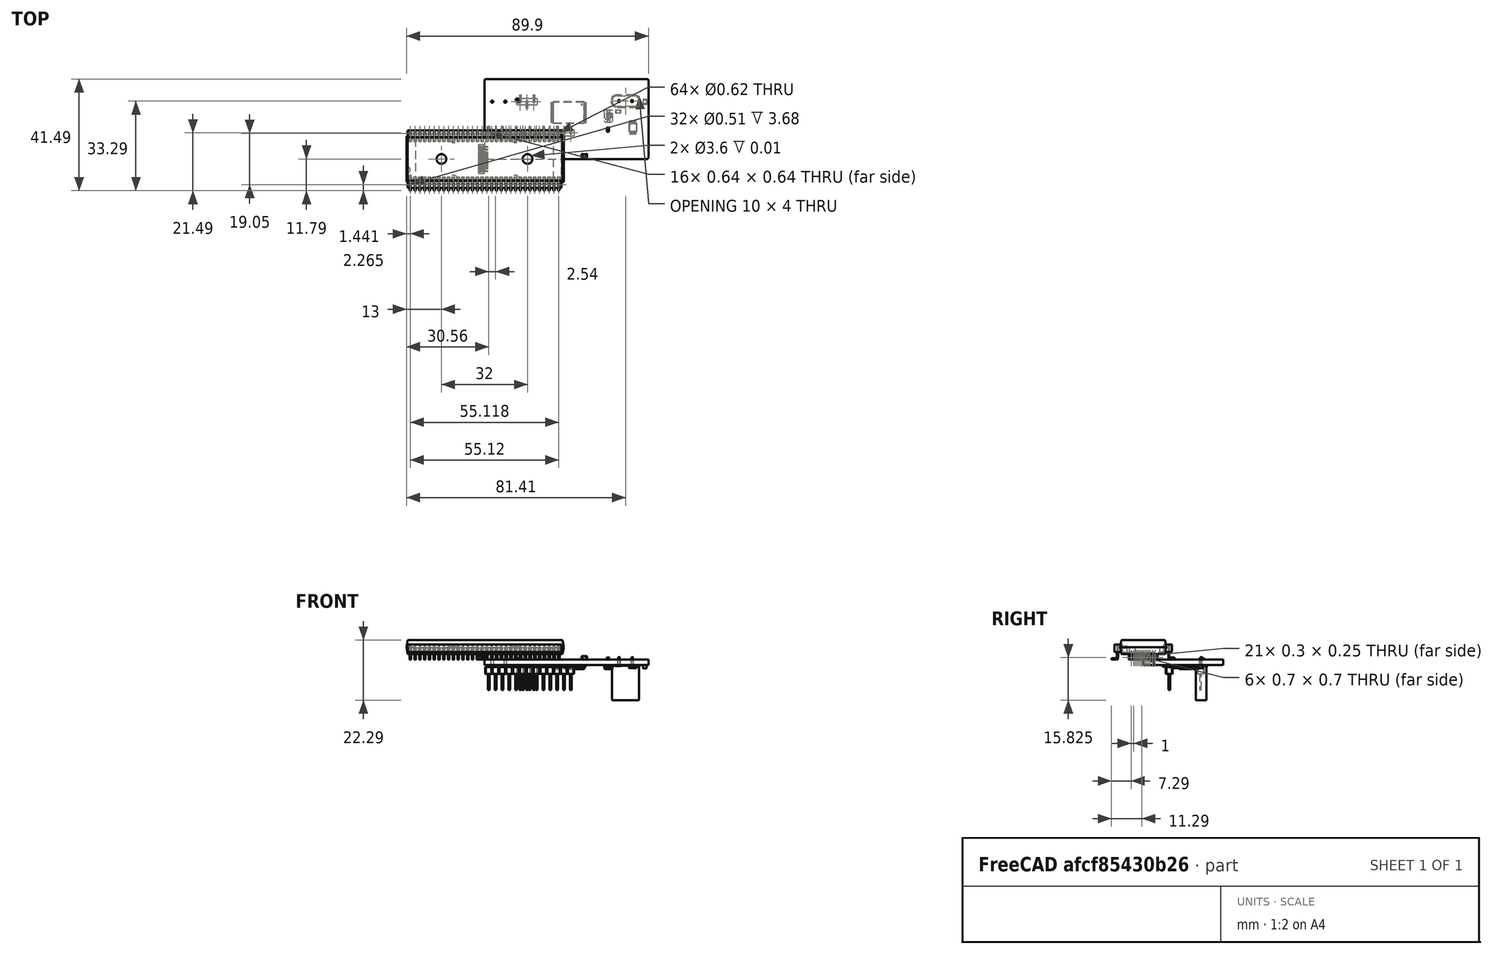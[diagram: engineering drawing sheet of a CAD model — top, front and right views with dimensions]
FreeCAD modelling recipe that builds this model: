
FCSTD DOCUMENT  (FreeCAD 0.20R29177 (Git))
Label: Ultra-MSX-VDP-socket-type
License: All rights reserved
LicenseURL: http://en.wikipedia.org/wiki/All_rights_reserved
objects: Part::Feature×145, App::Link×55, App::Part×24, PartDesign::CoordinateSystem×1, Sketcher::SketchObject×1
note: 147 computed .brp shape members not serialized (recipe doc carries the construction recipe); baked Part::Feature solids carry a one-line shape summary decoded from their .brp

FEATURE [PartDesign::CoordinateSystem] Local_CS_a649
  AttacherType = Attacher::AttachEngine3D
FEATURE [Part::Feature] Pcb_a649
  Placement = pos=(-95.1,117.3,0) rot=(0,0,1;0rad)
  shape: bbox 60.9 x 29.7 x 2 mm, 14 faces (baked)
FEATURE [Sketcher::SketchObject] PCB_Sketch_a649
  FullyConstrained = false
  sketch-geometry (8):
    g0: LineSegment StartX=60.4 StartY=29.7 StartZ=0 EndX=0.5 EndY=29.7 EndZ=0
    g1: LineSegment StartX=0 StartY=29.2 StartZ=0 EndX=1e-16 EndY=0.5 EndZ=0
    g2: LineSegment StartX=0.5 StartY=0 StartZ=0 EndX=60.4 EndY=-1.3e-15 EndZ=0
    g3: LineSegment StartX=60.9 StartY=0.5 StartZ=0 EndX=60.9 EndY=29.2 EndZ=0
    g4: ArcOfCircle CenterX=0.500001 CenterY=29.2 CenterZ=0 NormalX=0 NormalY=0 NormalZ=-1 AngleXU=2.66714e-06 Radius=0.500001 StartAngle=0 EndAngle=1.57079
    g5: ArcOfCircle CenterX=60.4 CenterY=0.500001 CenterZ=0 NormalX=0 NormalY=0 NormalZ=-1 AngleXU=-3.14159 Radius=0.500001 StartAngle=0 EndAngle=1.57079
    g6: ArcOfCircle CenterX=0.500001 CenterY=0.500001 CenterZ=0 NormalX=0 NormalY=0 NormalZ=-1 AngleXU=-1.57079 Radius=0.500001 StartAngle=0 EndAngle=1.57079
    g7: ArcOfCircle CenterX=60.4 CenterY=29.2 CenterZ=0 NormalX=0 NormalY=0 NormalZ=-1 AngleXU=1.5708 Radius=0.500001 StartAngle=0 EndAngle=1.57079
  constraints (8):
    c: Coincident(g1,g6)
    c: Coincident(g1,g4)
    c: Coincident(g2,g6)
    c: Coincident(g0,g4)
    c: Coincident(g2,g5)
    c: Coincident(g0,g7)
    c: Coincident(g3,g5)
    c: Coincident(g3,g7)
FEATURE [Part::Feature] Part__Feature  label="base-pin002"
  shape: bbox 0.62 x 2.57 x 5.591 mm, 71 faces (baked)
FEATURE [Part::Feature] Part__Feature001  label="base-pin003"
  Placement = pos=(1.778,0,0) rot=(0,0,1;0rad)
  shape: bbox 0.62 x 2.57 x 5.591 mm, 71 faces (baked)
FEATURE [Part::Feature] Part__Feature002  label="base-pin004"
  Placement = pos=(3.556,0,0) rot=(0,0,1;0rad)
  shape: bbox 0.62 x 2.57 x 5.591 mm, 71 faces (baked)
FEATURE [Part::Feature] Part__Feature003  label="base-pin005"
  Placement = pos=(5.334,0,0) rot=(0,0,1;0rad)
  shape: bbox 0.62 x 2.57 x 5.591 mm, 71 faces (baked)
FEATURE [Part::Feature] Part__Feature004  label="base-pin006"
  Placement = pos=(7.112,0,0) rot=(0,0,1;0rad)
  shape: bbox 0.62 x 2.57 x 5.591 mm, 71 faces (baked)
FEATURE [Part::Feature] Part__Feature005  label="base-pin007"
  Placement = pos=(8.89,0,0) rot=(0,0,1;0rad)
  shape: bbox 0.62 x 2.57 x 5.591 mm, 71 faces (baked)
FEATURE [Part::Feature] Part__Feature006  label="base-pin008"
  Placement = pos=(10.668,0,0) rot=(0,0,1;0rad)
  shape: bbox 0.62 x 2.57 x 5.591 mm, 71 faces (baked)
FEATURE [Part::Feature] Part__Feature007  label="base-pin009"
  Placement = pos=(12.446,0,0) rot=(0,0,1;0rad)
  shape: bbox 0.62 x 2.57 x 5.591 mm, 71 faces (baked)
FEATURE [Part::Feature] Part__Feature008  label="base-pin010"
  Placement = pos=(14.224,0,0) rot=(0,0,1;0rad)
  shape: bbox 0.62 x 2.57 x 5.591 mm, 71 faces (baked)
FEATURE [Part::Feature] Part__Feature009  label="base-pin011"
  Placement = pos=(16.002,0,0) rot=(0,0,1;0rad)
  shape: bbox 0.62 x 2.57 x 5.591 mm, 71 faces (baked)
FEATURE [Part::Feature] Part__Feature010  label="base-pin012"
  Placement = pos=(17.78,0,0) rot=(0,0,1;0rad)
  shape: bbox 0.62 x 2.57 x 5.591 mm, 71 faces (baked)
FEATURE [Part::Feature] Part__Feature011  label="base-pin013"
  Placement = pos=(19.558,0,0) rot=(0,0,1;0rad)
  shape: bbox 0.62 x 2.57 x 5.591 mm, 71 faces (baked)
FEATURE [Part::Feature] Part__Feature012  label="base-pin014"
  Placement = pos=(21.336,0,0) rot=(0,0,1;0rad)
  shape: bbox 0.62 x 2.57 x 5.591 mm, 71 faces (baked)
FEATURE [Part::Feature] Part__Feature013  label="base-pin015"
  Placement = pos=(23.114,0,0) rot=(0,0,1;0rad)
  shape: bbox 0.62 x 2.57 x 5.591 mm, 71 faces (baked)
FEATURE [Part::Feature] Part__Feature014  label="base-pin016"
  Placement = pos=(24.892,0,0) rot=(0,0,1;0rad)
  shape: bbox 0.62 x 2.57 x 5.591 mm, 71 faces (baked)
FEATURE [Part::Feature] Part__Feature015  label="base-pin017"
  Placement = pos=(26.67,0,0) rot=(0,0,1;0rad)
  shape: bbox 0.62 x 2.57 x 5.591 mm, 71 faces (baked)
FEATURE [Part::Feature] Part__Feature016  label="base-pin018"
  Placement = pos=(28.448,0,0) rot=(0,0,1;0rad)
  shape: bbox 0.62 x 2.57 x 5.591 mm, 71 faces (baked)
FEATURE [Part::Feature] Part__Feature017  label="base-pin019"
  Placement = pos=(30.226,0,0) rot=(0,0,1;0rad)
  shape: bbox 0.62 x 2.57 x 5.591 mm, 71 faces (baked)
FEATURE [Part::Feature] Part__Feature018  label="base-pin020"
  Placement = pos=(32.004,0,0) rot=(0,0,1;0rad)
  shape: bbox 0.62 x 2.57 x 5.591 mm, 71 faces (baked)
FEATURE [Part::Feature] Part__Feature019  label="base-pin021"
  Placement = pos=(33.782,0,0) rot=(0,0,1;0rad)
  shape: bbox 0.62 x 2.57 x 5.591 mm, 71 faces (baked)
FEATURE [Part::Feature] Part__Feature020  label="base-pin022"
  Placement = pos=(35.56,0,0) rot=(0,0,1;0rad)
  shape: bbox 0.62 x 2.57 x 5.591 mm, 71 faces (baked)
FEATURE [Part::Feature] Part__Feature021  label="base-pin023"
  Placement = pos=(37.338,0,0) rot=(0,0,1;0rad)
  shape: bbox 0.62 x 2.57 x 5.591 mm, 71 faces (baked)
FEATURE [Part::Feature] Part__Feature022  label="base-pin024"
  Placement = pos=(39.116,0,0) rot=(0,0,1;0rad)
  shape: bbox 0.62 x 2.57 x 5.591 mm, 71 faces (baked)
FEATURE [Part::Feature] Part__Feature023  label="base-pin025"
  Placement = pos=(40.894,0,0) rot=(0,0,1;0rad)
  shape: bbox 0.62 x 2.57 x 5.591 mm, 71 faces (baked)
FEATURE [Part::Feature] Part__Feature024  label="base-pin026"
  Placement = pos=(42.672,0,0) rot=(0,0,1;0rad)
  shape: bbox 0.62 x 2.57 x 5.591 mm, 71 faces (baked)
FEATURE [Part::Feature] Part__Feature025  label="base-pin027"
  Placement = pos=(44.45,0,0) rot=(0,0,1;0rad)
  shape: bbox 0.62 x 2.57 x 5.591 mm, 71 faces (baked)
FEATURE [Part::Feature] Part__Feature026  label="base-pin028"
  Placement = pos=(46.228,0,0) rot=(0,0,1;0rad)
  shape: bbox 0.62 x 2.57 x 5.591 mm, 71 faces (baked)
FEATURE [Part::Feature] Part__Feature027  label="base-pin029"
  Placement = pos=(48.006,0,0) rot=(0,0,1;0rad)
  shape: bbox 0.62 x 2.57 x 5.591 mm, 71 faces (baked)
FEATURE [Part::Feature] Part__Feature028  label="base-pin030"
  Placement = pos=(49.784,0,0) rot=(0,0,1;0rad)
  shape: bbox 0.62 x 2.57 x 5.591 mm, 71 faces (baked)
FEATURE [Part::Feature] Part__Feature029  label="base-pin031"
  Placement = pos=(51.562,0,0) rot=(0,0,1;0rad)
  shape: bbox 0.62 x 2.57 x 5.591 mm, 71 faces (baked)
FEATURE [Part::Feature] Part__Feature030  label="base-pin032"
  Placement = pos=(53.34,0,0) rot=(0,0,1;0rad)
  shape: bbox 0.62 x 2.57 x 5.591 mm, 71 faces (baked)
FEATURE [Part::Feature] Part__Feature031  label="base-pin033"
  Placement = pos=(55.118,0,0) rot=(0,0,1;0rad)
  shape: bbox 0.62 x 2.57 x 5.591 mm, 71 faces (baked)
FEATURE [App::Part] top_pins  label="top-pins"
  Group = -> [Part__Feature,Part__Feature001,Part__Feature002,Part__Feature003,Part__Feature004,Part__Feature005,Part__Feature006,Part__Feature007,Part__Feature008,Part__Feature009,Part__Feature010,Part__Feature011,Part__Feature012,Part__Feature013,Part__Feature014,Part__Feature015,Part__Feature016,Part__Feature017,Part__Feature018,Part__Feature019,Part__Feature020,Part__Feature021,Part__Feature022,+9 more]
  Origin = -> Origin008
  Placement = pos=(0,0,0) rot=(0,0,1;3.14159rad)
FEATURE [Part::Feature] Part__Feature032  label="base-pin1"
  shape: bbox 0.62 x 2.57 x 5.591 mm, 71 faces (baked)
FEATURE [Part::Feature] Part__Feature033  label="base-pin034"
  Placement = pos=(1.778,0,0) rot=(0,0,1;0rad)
  shape: bbox 0.62 x 2.57 x 5.591 mm, 71 faces (baked)
FEATURE [Part::Feature] Part__Feature034  label="base-pin035"
  Placement = pos=(3.556,0,0) rot=(0,0,1;0rad)
  shape: bbox 0.62 x 2.57 x 5.591 mm, 71 faces (baked)
FEATURE [Part::Feature] Part__Feature035  label="base-pin036"
  Placement = pos=(5.334,0,0) rot=(0,0,1;0rad)
  shape: bbox 0.62 x 2.57 x 5.591 mm, 71 faces (baked)
FEATURE [Part::Feature] Part__Feature036  label="base-pin037"
  Placement = pos=(7.112,0,0) rot=(0,0,1;0rad)
  shape: bbox 0.62 x 2.57 x 5.591 mm, 71 faces (baked)
FEATURE [Part::Feature] Part__Feature037  label="base-pin038"
  Placement = pos=(8.89,0,0) rot=(0,0,1;0rad)
  shape: bbox 0.62 x 2.57 x 5.591 mm, 71 faces (baked)
FEATURE [Part::Feature] Part__Feature038  label="base-pin039"
  Placement = pos=(10.668,0,0) rot=(0,0,1;0rad)
  shape: bbox 0.62 x 2.57 x 5.591 mm, 71 faces (baked)
FEATURE [Part::Feature] Part__Feature039  label="base-pin040"
  Placement = pos=(12.446,0,0) rot=(0,0,1;0rad)
  shape: bbox 0.62 x 2.57 x 5.591 mm, 71 faces (baked)
FEATURE [Part::Feature] Part__Feature040  label="base-pin041"
  Placement = pos=(14.224,0,0) rot=(0,0,1;0rad)
  shape: bbox 0.62 x 2.57 x 5.591 mm, 71 faces (baked)
FEATURE [Part::Feature] Part__Feature041  label="base-pin042"
  Placement = pos=(16.002,0,0) rot=(0,0,1;0rad)
  shape: bbox 0.62 x 2.57 x 5.591 mm, 71 faces (baked)
FEATURE [Part::Feature] Part__Feature042  label="base-pin043"
  Placement = pos=(17.78,0,0) rot=(0,0,1;0rad)
  shape: bbox 0.62 x 2.57 x 5.591 mm, 71 faces (baked)
FEATURE [Part::Feature] Part__Feature043  label="base-pin044"
  Placement = pos=(19.558,0,0) rot=(0,0,1;0rad)
  shape: bbox 0.62 x 2.57 x 5.591 mm, 71 faces (baked)
FEATURE [Part::Feature] Part__Feature044  label="base-pin045"
  Placement = pos=(21.336,0,0) rot=(0,0,1;0rad)
  shape: bbox 0.62 x 2.57 x 5.591 mm, 71 faces (baked)
FEATURE [Part::Feature] Part__Feature045  label="base-pin046"
  Placement = pos=(23.114,0,0) rot=(0,0,1;0rad)
  shape: bbox 0.62 x 2.57 x 5.591 mm, 71 faces (baked)
FEATURE [Part::Feature] Part__Feature046  label="base-pin047"
  Placement = pos=(24.892,0,0) rot=(0,0,1;0rad)
  shape: bbox 0.62 x 2.57 x 5.591 mm, 71 faces (baked)
FEATURE [Part::Feature] Part__Feature047  label="base-pin048"
  Placement = pos=(26.67,0,0) rot=(0,0,1;0rad)
  shape: bbox 0.62 x 2.57 x 5.591 mm, 71 faces (baked)
FEATURE [Part::Feature] Part__Feature048  label="base-pin049"
  Placement = pos=(28.448,0,0) rot=(0,0,1;0rad)
  shape: bbox 0.62 x 2.57 x 5.591 mm, 71 faces (baked)
FEATURE [Part::Feature] Part__Feature049  label="base-pin050"
  Placement = pos=(30.226,0,0) rot=(0,0,1;0rad)
  shape: bbox 0.62 x 2.57 x 5.591 mm, 71 faces (baked)
FEATURE [Part::Feature] Part__Feature050  label="base-pin051"
  Placement = pos=(32.004,0,0) rot=(0,0,1;0rad)
  shape: bbox 0.62 x 2.57 x 5.591 mm, 71 faces (baked)
FEATURE [Part::Feature] Part__Feature051  label="base-pin052"
  Placement = pos=(33.782,0,0) rot=(0,0,1;0rad)
  shape: bbox 0.62 x 2.57 x 5.591 mm, 71 faces (baked)
FEATURE [Part::Feature] Part__Feature052  label="base-pin053"
  Placement = pos=(35.56,0,0) rot=(0,0,1;0rad)
  shape: bbox 0.62 x 2.57 x 5.591 mm, 71 faces (baked)
FEATURE [Part::Feature] Part__Feature053  label="base-pin054"
  Placement = pos=(37.338,0,0) rot=(0,0,1;0rad)
  shape: bbox 0.62 x 2.57 x 5.591 mm, 71 faces (baked)
FEATURE [Part::Feature] Part__Feature054  label="base-pin055"
  Placement = pos=(39.116,0,0) rot=(0,0,1;0rad)
  shape: bbox 0.62 x 2.57 x 5.591 mm, 71 faces (baked)
FEATURE [Part::Feature] Part__Feature055  label="base-pin056"
  Placement = pos=(40.894,0,0) rot=(0,0,1;0rad)
  shape: bbox 0.62 x 2.57 x 5.591 mm, 71 faces (baked)
FEATURE [Part::Feature] Part__Feature056  label="base-pin057"
  Placement = pos=(42.672,0,0) rot=(0,0,1;0rad)
  shape: bbox 0.62 x 2.57 x 5.591 mm, 71 faces (baked)
FEATURE [Part::Feature] Part__Feature057  label="base-pin058"
  Placement = pos=(44.45,0,0) rot=(0,0,1;0rad)
  shape: bbox 0.62 x 2.57 x 5.591 mm, 71 faces (baked)
FEATURE [Part::Feature] Part__Feature058  label="base-pin059"
  Placement = pos=(46.228,0,0) rot=(0,0,1;0rad)
  shape: bbox 0.62 x 2.57 x 5.591 mm, 71 faces (baked)
FEATURE [Part::Feature] Part__Feature059  label="base-pin060"
  Placement = pos=(48.006,0,0) rot=(0,0,1;0rad)
  shape: bbox 0.62 x 2.57 x 5.591 mm, 71 faces (baked)
FEATURE [Part::Feature] Part__Feature060  label="base-pin061"
  Placement = pos=(49.784,0,0) rot=(0,0,1;0rad)
  shape: bbox 0.62 x 2.57 x 5.591 mm, 71 faces (baked)
FEATURE [Part::Feature] Part__Feature061  label="base-pin062"
  Placement = pos=(51.562,0,0) rot=(0,0,1;0rad)
  shape: bbox 0.62 x 2.57 x 5.591 mm, 71 faces (baked)
FEATURE [Part::Feature] Part__Feature062  label="base-pin063"
  Placement = pos=(53.34,0,0) rot=(0,0,1;0rad)
  shape: bbox 0.62 x 2.57 x 5.591 mm, 71 faces (baked)
FEATURE [Part::Feature] Part__Feature063  label="base-pin064"
  Placement = pos=(55.118,0,0) rot=(0,0,1;0rad)
  shape: bbox 0.62 x 2.57 x 5.591 mm, 71 faces (baked)
FEATURE [App::Part] bot_pins  label="bot-pins"
  Group = -> [Part__Feature032,Part__Feature033,Part__Feature034,Part__Feature035,Part__Feature036,Part__Feature037,Part__Feature038,Part__Feature039,Part__Feature040,Part__Feature041,Part__Feature042,Part__Feature043,Part__Feature044,Part__Feature045,Part__Feature046,Part__Feature047,Part__Feature048,Part__Feature049,Part__Feature050,Part__Feature051,Part__Feature052,Part__Feature053,Part__Feature054,+9 more]
  Origin = -> Origin009
FEATURE [App::Part] Pins
  Group = -> [top_pins,bot_pins]
  Origin = -> Origin010
FEATURE [Part::Feature] Part__Feature064  label="Plastic"
  shape: bbox 57.2 x 21.34 x 2.79 mm, 105 faces (baked)
FEATURE [App::Part] Mill_Max_117_43  label="U3_Mill_Max_117_43_7bad8f66661d[2]"
  Group = -> [Pins,Part__Feature064]
  Origin = -> Origin011
  Placement = pos=(31.2,16.45,0) rot=(0,0,1;0rad)
FEATURE [Part::Feature] Shape  label="C6_C_0603_1608Metric_e4ffc2d5bdca"
  Placement = pos=(45.865,10.865,0) rot=(0,0,1;1.5708rad)
  shape: bbox 0.8 x 1.6 x 0.8 mm, 28 faces (baked)
FEATURE [Part::Feature] Shape001  label="R1_R_0603_1608Metric_ed6f3b55dae2"
  Placement = pos=(12.4,21.75,0) rot=(0,0,1;2.35619rad)
  shape: bbox 1.697 x 1.697 x 0.45 mm, 26 faces (baked)
FEATURE [App::Link] R1_R_0603_1608Metric_ed6f3b55dae2_ln_  label="R82_R_0603_1608Metric_d4caecac030a"
  LinkPlacement = pos=(44.3,12.6,0) rot=(0,0,1;1.5708rad)
  LinkedObject = -> Shape001
  Placement = pos=(44.3,12.6,0) rot=(0,0,1;1.5708rad)
FEATURE [App::Link] R1_R_0603_1608Metric_ed6f3b55dae2_ln_001  label="R5_R_0603_1608Metric_b329b1c24be4"
  LinkPlacement = pos=(16.8,22.075,0) rot=(0,0,1;1.5708rad)
  LinkedObject = -> Shape001
  Placement = pos=(16.8,22.075,0) rot=(0,0,1;1.5708rad)
FEATURE [App::Link] R1_R_0603_1608Metric_ed6f3b55dae2_ln_002  label="R12_R_0603_1608Metric_2195333ff90b"
  LinkPlacement = pos=(14.2,12.6,0) rot=(0,0,-1;1.5708rad)
  LinkedObject = -> Shape001
  Placement = pos=(14.2,12.6,0) rot=(0,0,-1;1.5708rad)
FEATURE [App::Link] R1_R_0603_1608Metric_ed6f3b55dae2_ln_003  label="R81_R_0603_1608Metric_e3e91bc86c1a"
  LinkPlacement = pos=(47.365,11.265,0) rot=(0,0,1;1.5708rad)
  LinkedObject = -> Shape001
  Placement = pos=(47.365,11.265,0) rot=(0,0,1;1.5708rad)
FEATURE [App::Link] R1_R_0603_1608Metric_ed6f3b55dae2_ln_004  label="R20_R_0603_1608Metric_7d7dade67ea7"
  LinkPlacement = pos=(24.3,12.1,0) rot=(0,0,1;3.14159rad)
  LinkedObject = -> Shape001
  Placement = pos=(24.3,12.1,0) rot=(0,0,1;3.14159rad)
FEATURE [App::Link] C6_C_0603_1608Metric_e4ffc2d5bdca_ln_  label="C16_C_0603_1608Metric_4bdb616e9b66"
  LinkPlacement = pos=(38.1,10.2,0) rot=(0,0,1;0rad)
  LinkedObject = -> Shape
  Placement = pos=(38.1,10.2,0) rot=(0,0,1;0rad)
FEATURE [App::Link] R1_R_0603_1608Metric_ed6f3b55dae2_ln_005  label="R10_R_0603_1608Metric_ed460fd84905"
  LinkPlacement = pos=(12.4,2.2,0) rot=(0,0,-1;1.5708rad)
  LinkedObject = -> Shape001
  Placement = pos=(12.4,2.2,0) rot=(0,0,-1;1.5708rad)
FEATURE [App::Link] C6_C_0603_1608Metric_e4ffc2d5bdca_ln_001  label="C8_C_0603_1608Metric_43c608d33d12"
  LinkPlacement = pos=(42.8,12.6,0) rot=(0,0,1;1.5708rad)
  LinkedObject = -> Shape
  Placement = pos=(42.8,12.6,0) rot=(0,0,1;1.5708rad)
FEATURE [Part::Feature] Shape002  label="L3_L_0805_2012Metric_7024b431f41a"
  Placement = pos=(37.1,1.2,0) rot=(0,0,1;0rad)
  shape: bbox 2 x 1.25 x 1.25 mm, 28 faces (baked)
FEATURE [App::Link] R1_R_0603_1608Metric_ed6f3b55dae2_ln_006  label="R84_R_0603_1608Metric_7d963f7814c4"
  LinkPlacement = pos=(10.7,2.2,0) rot=(0,0,-1;1.5708rad)
  LinkedObject = -> Shape001
  Placement = pos=(10.7,2.2,0) rot=(0,0,-1;1.5708rad)
FEATURE [App::Link] R1_R_0603_1608Metric_ed6f3b55dae2_ln_007  label="R83_R_0603_1608Metric_5f107b2ae899"
  LinkPlacement = pos=(38.2,11.7,0) rot=(0,0,1;3.14159rad)
  LinkedObject = -> Shape001
  Placement = pos=(38.2,11.7,0) rot=(0,0,1;3.14159rad)
FEATURE [App::Link] R1_R_0603_1608Metric_ed6f3b55dae2_ln_008  label="R60_R_0603_1608Metric_ee9b7d5e1906"
  LinkPlacement = pos=(37.4,2.8,0) rot=(0,0,1;0rad)
  LinkedObject = -> Shape001
  Placement = pos=(37.4,2.8,0) rot=(0,0,1;0rad)
FEATURE [App::Link] C6_C_0603_1608Metric_e4ffc2d5bdca_ln_002  label="C7_C_0603_1608Metric_cf974e6831ff"
  LinkPlacement = pos=(40.9,12.625,0) rot=(0,0,1;1.5708rad)
  LinkedObject = -> Shape
  Placement = pos=(40.9,12.625,0) rot=(0,0,1;1.5708rad)
FEATURE [App::Link] R1_R_0603_1608Metric_ed6f3b55dae2_ln_009  label="R58_R_0603_1608Metric_b9a300878665"
  LinkPlacement = pos=(14.4,22,0) rot=(0,0,-1;0.785398rad)
  LinkedObject = -> Shape001
  Placement = pos=(14.4,22,0) rot=(0,0,-1;0.785398rad)
FEATURE [App::Link] C6_C_0603_1608Metric_e4ffc2d5bdca_ln_003  label="C11_C_0603_1608Metric_38beb4399a59"
  LinkPlacement = pos=(46.1,1.75,0) rot=(0,0,1;1.5708rad)
  LinkedObject = -> Shape
  Placement = pos=(46.1,1.75,0) rot=(0,0,1;1.5708rad)
FEATURE [App::Link] R1_R_0603_1608Metric_ed6f3b55dae2_ln_010  label="R27_R_0603_1608Metric_a411e8e7a906"
  LinkPlacement = pos=(57.3,7.7,-2) rot=(0,1,0;3.14159rad)
  LinkedObject = -> Shape001
  Placement = pos=(57.3,7.7,-2) rot=(0,1,0;3.14159rad)
FEATURE [App::Link] R1_R_0603_1608Metric_ed6f3b55dae2_ln_011  label="R14_R_0603_1608Metric_b666e58988c9"
  LinkPlacement = pos=(40.7,3.6,-2) rot=(0.707107,0.707107,0;3.14159rad)
  LinkedObject = -> Shape001
  Placement = pos=(40.7,3.6,-2) rot=(0.707107,0.707107,0;3.14159rad)
FEATURE [App::Link] R1_R_0603_1608Metric_ed6f3b55dae2_ln_012  label="R53_R_0603_1608Metric_dd796e6052a9"
  LinkPlacement = pos=(13.55,5.8,-2) rot=(0,1,0;3.14159rad)
  LinkedObject = -> Shape001
  Placement = pos=(13.55,5.8,-2) rot=(0,1,0;3.14159rad)
FEATURE [App::Link] C6_C_0603_1608Metric_e4ffc2d5bdca_ln_004  label="C15_C_0603_1608Metric_af0c3dbdae54"
  LinkPlacement = pos=(57.7,11.6,-2) rot=(0.707107,-0.707107,0;3.14159rad)
  LinkedObject = -> Shape
  Placement = pos=(57.7,11.6,-2) rot=(0.707107,-0.707107,0;3.14159rad)
FEATURE [App::Link] R1_R_0603_1608Metric_ed6f3b55dae2_ln_013  label="R21_R_0603_1608Metric_f35c04f488f9"
  LinkPlacement = pos=(49.2,8.7,-2) rot=(1,0,0;3.14159rad)
  LinkedObject = -> Shape001
  Placement = pos=(49.2,8.7,-2) rot=(1,0,0;3.14159rad)
FEATURE [Part::Feature] Shape003  label="R4_R_0805_2012Metric_f107bcb44f6e"
  Placement = pos=(49.5875,17.65,-2) rot=(1,0,0;3.14159rad)
  shape: bbox 2 x 1.2 x 0.45 mm, 26 faces (baked)
FEATURE [App::Link] R1_R_0603_1608Metric_ed6f3b55dae2_ln_014  label="R23_R_0603_1608Metric_cfb541b6819d"
  LinkPlacement = pos=(34.4,10.7,-2) rot=(0.707107,0.707107,0;3.14159rad)
  LinkedObject = -> Shape001
  Placement = pos=(34.4,10.7,-2) rot=(0.707107,0.707107,0;3.14159rad)
FEATURE [App::Link] R1_R_0603_1608Metric_ed6f3b55dae2_ln_015  label="R15_R_0603_1608Metric_62d8d2cdaec6"
  LinkPlacement = pos=(44,1.7,-2) rot=(0.707107,-0.707107,0;3.14159rad)
  LinkedObject = -> Shape001
  Placement = pos=(44,1.7,-2) rot=(0.707107,-0.707107,0;3.14159rad)
FEATURE [Part::Feature] Shape004  label="U6_VSSOP_10_3x3mm_P05mm_53867965ed20"
  Placement = pos=(55.15,11.7,-2) rot=(0.707107,-0.707107,0;3.14159rad)
  shape: bbox 3 x 4.9 x 1.2 mm, 186 faces (baked)
FEATURE [Part::Feature] Shape005  label="C3_C_0805_2012Metric_be4dabc485b9"
  Placement = pos=(59.55,21.2,-2) rot=(0.707107,-0.707107,0;3.14159rad)
  shape: bbox 1.25 x 2 x 1.25 mm, 28 faces (baked)
FEATURE [App::Link] L3_L_0805_2012Metric_7024b431f41a_ln_  label="L1_L_0805_2012Metric_dcb766a75268"
  LinkPlacement = pos=(57.8,15,-2) rot=(0.707107,0.707107,0;3.14159rad)
  LinkedObject = -> Shape002
  Placement = pos=(57.8,15,-2) rot=(0.707107,0.707107,0;3.14159rad)
FEATURE [App::Link] R1_R_0603_1608Metric_ed6f3b55dae2_ln_016  label="R49_R_0603_1608Metric_953d89943b0f"
  LinkPlacement = pos=(31.9,7.3,-2) rot=(1,0,0;3.14159rad)
  LinkedObject = -> Shape001
  Placement = pos=(31.9,7.3,-2) rot=(1,0,0;3.14159rad)
FEATURE [Part::Feature] Shape006  label="U14_TSOP_I_28_118x8mm_P055mm_c181658d2376"
  Placement = pos=(31.3,17.25,-2) rot=(0,1,0;3.14159rad)
  shape: bbox 13.2 x 8 x 1.6 mm, 456 faces (baked)
FEATURE [Part::Feature] Shape007  label="Y3_Crystal_HC49-U_Vertical_0fe1bbda450f"
  Placement = pos=(54.85,21.5,-2) rot=(0,1,0;3.14159rad)
  shape: bbox 10.9 x 4.65 x 16 mm, 26 faces (baked)
FEATURE [App::Link] R4_R_0805_2012Metric_f107bcb44f6e_ln_  label="R2_R_0805_2012Metric_293fb1e13199"
  LinkPlacement = pos=(6.3,17.6,-2) rot=(1,0,0;3.14159rad)
  LinkedObject = -> Shape003
  Placement = pos=(6.3,17.6,-2) rot=(1,0,0;3.14159rad)
FEATURE [Part::Feature] Shape008  label="C5_Sprague_Goodman_SGC3_37e8c659f2e6"
  Placement = pos=(46.025,15.9,-2) rot=(0.707107,0.707107,0;3.14159rad)
  shape: bbox 3.247 x 4.625 x 1.5 mm, 36 faces (baked)
FEATURE [App::Link] R1_R_0603_1608Metric_ed6f3b55dae2_ln_017  label="R61_R_0603_1608Metric_2d9e7edbb70d"
  LinkPlacement = pos=(58.75,9.175,-2) rot=(0,1,0;3.14159rad)
  LinkedObject = -> Shape001
  Placement = pos=(58.75,9.175,-2) rot=(0,1,0;3.14159rad)
FEATURE [App::Link] R1_R_0603_1608Metric_ed6f3b55dae2_ln_018  label="R7_R_0603_1608Metric_b15c88e18e3f"
  LinkPlacement = pos=(23.1,22.1,-2) rot=(1,0,0;3.14159rad)
  LinkedObject = -> Shape001
  Placement = pos=(23.1,22.1,-2) rot=(1,0,0;3.14159rad)
FEATURE [App::Link] R1_R_0603_1608Metric_ed6f3b55dae2_ln_019  label="R54_R_0603_1608Metric_722876daf014"
  LinkPlacement = pos=(21.55,6.55,-2) rot=(0,1,0;3.14159rad)
  LinkedObject = -> Shape001
  Placement = pos=(21.55,6.55,-2) rot=(0,1,0;3.14159rad)
FEATURE [App::Link] R1_R_0603_1608Metric_ed6f3b55dae2_ln_020  label="R6_R_0603_1608Metric_8a82445061e6"
  LinkPlacement = pos=(31.45,22.35,-2) rot=(0,1,0;3.14159rad)
  LinkedObject = -> Shape001
  Placement = pos=(31.45,22.35,-2) rot=(0,1,0;3.14159rad)
FEATURE [App::Link] C5_Sprague_Goodman_SGC3_37e8c659f2e6_ln_  label="C1_Sprague_Goodman_SGC3_dd31bb1523f4"
  LinkPlacement = pos=(4.5,14.75,-2) rot=(1,0,0;3.14159rad)
  LinkedObject = -> Shape008
  Placement = pos=(4.5,14.75,-2) rot=(1,0,0;3.14159rad)
FEATURE [App::Link] C6_C_0603_1608Metric_e4ffc2d5bdca_ln_005  label="C2_C_0603_1608Metric_0b1b18837ebd"
  LinkPlacement = pos=(3.1,17.8,-2) rot=(1,0,0;3.14159rad)
  LinkedObject = -> Shape
  Placement = pos=(3.1,17.8,-2) rot=(1,0,0;3.14159rad)
FEATURE [App::Link] R1_R_0603_1608Metric_ed6f3b55dae2_ln_021  label="R57_R_0603_1608Metric_aec65f8ff485"
  LinkPlacement = pos=(9.5,12.1,-2) rot=(0,1,0;3.14159rad)
  LinkedObject = -> Shape001
  Placement = pos=(9.5,12.1,-2) rot=(0,1,0;3.14159rad)
FEATURE [App::Link] C3_C_0805_2012Metric_be4dabc485b9_ln_  label="C73_C_0805_2012Metric_05153e2cdc69"
  LinkPlacement = pos=(56.2,17.8,-2) rot=(0,1,0;3.14159rad)
  LinkedObject = -> Shape005
  Placement = pos=(56.2,17.8,-2) rot=(0,1,0;3.14159rad)
FEATURE [App::Link] R1_R_0603_1608Metric_ed6f3b55dae2_ln_022  label="R13_R_0603_1608Metric_307ab71b2f2b"
  LinkPlacement = pos=(42.5,3.65,-2) rot=(0.707107,0.707107,0;3.14159rad)
  LinkedObject = -> Shape001
  Placement = pos=(42.5,3.65,-2) rot=(0.707107,0.707107,0;3.14159rad)
FEATURE [App::Link] C6_C_0603_1608Metric_e4ffc2d5bdca_ln_006  label="C19_C_0603_1608Metric_ba66b0bf55ae"
  LinkPlacement = pos=(59.4,11.8,-2) rot=(0.707107,0.707107,0;3.14159rad)
  LinkedObject = -> Shape
  Placement = pos=(59.4,11.8,-2) rot=(0.707107,0.707107,0;3.14159rad)
FEATURE [App::Link] R1_R_0603_1608Metric_ed6f3b55dae2_ln_023  label="R51_R_0603_1608Metric_7bd6d0df39b7"
  LinkPlacement = pos=(19.5,12.1,-2) rot=(1,0,0;3.14159rad)
  LinkedObject = -> Shape001
  Placement = pos=(19.5,12.1,-2) rot=(1,0,0;3.14159rad)
FEATURE [App::Link] R1_R_0603_1608Metric_ed6f3b55dae2_ln_024  label="R22_R_0603_1608Metric_cb1c37444e2f"
  LinkPlacement = pos=(52.6,8.2125,-2) rot=(0.707107,0.707107,0;3.14159rad)
  LinkedObject = -> Shape001
  Placement = pos=(52.6,8.2125,-2) rot=(0.707107,0.707107,0;3.14159rad)
FEATURE [App::Link] C6_C_0603_1608Metric_e4ffc2d5bdca_ln_007  label="C12_C_0603_1608Metric_32ee04979fd2"
  LinkPlacement = pos=(52.55,11.925,-2) rot=(0.707107,0.707107,0;3.14159rad)
  LinkedObject = -> Shape
  Placement = pos=(52.55,11.925,-2) rot=(0.707107,0.707107,0;3.14159rad)
FEATURE [App::Link] C6_C_0603_1608Metric_e4ffc2d5bdca_ln_008  label="C10_C_0603_1608Metric_ed01532d6a4e"
  LinkPlacement = pos=(39.9,6.8,-2) rot=(0.707107,0.707107,0;3.14159rad)
  LinkedObject = -> Shape
  Placement = pos=(39.9,6.8,-2) rot=(0.707107,0.707107,0;3.14159rad)
FEATURE [App::Link] R1_R_0603_1608Metric_ed6f3b55dae2_ln_025  label="R56_R_0603_1608Metric_1c0ae7ad8c6e"
  LinkPlacement = pos=(1.9,7.3,-2) rot=(0,1,0;3.14159rad)
  LinkedObject = -> Shape001
  Placement = pos=(1.9,7.3,-2) rot=(0,1,0;3.14159rad)
FEATURE [App::Link] R1_R_0603_1608Metric_ed6f3b55dae2_ln_026  label="R50_R_0603_1608Metric_f5e2b95ccbbe"
  LinkPlacement = pos=(29.8,12.05,-2) rot=(0,1,0;3.14159rad)
  LinkedObject = -> Shape001
  Placement = pos=(29.8,12.05,-2) rot=(0,1,0;3.14159rad)
FEATURE [App::Link] C6_C_0603_1608Metric_e4ffc2d5bdca_ln_009  label="C17_C_0603_1608Metric_ba9556bdb5b0"
  LinkPlacement = pos=(54.95,15.7,-2) rot=(0,1,0;3.14159rad)
  LinkedObject = -> Shape
  Placement = pos=(54.95,15.7,-2) rot=(0,1,0;3.14159rad)
FEATURE [App::Link] R1_R_0603_1608Metric_ed6f3b55dae2_ln_027  label="R25_R_0603_1608Metric_d3d0e9069176"
  LinkPlacement = pos=(34,6.35,-2) rot=(-0.382683,0.92388,0;3.14159rad)
  LinkedObject = -> Shape001
  Placement = pos=(34,6.35,-2) rot=(-0.382683,0.92388,0;3.14159rad)
FEATURE [App::Link] C6_C_0603_1608Metric_e4ffc2d5bdca_ln_010  label="C18_C_0603_1608Metric_0a9993050c82"
  LinkPlacement = pos=(59.4,15.4,-2) rot=(0.707107,0.707107,0;3.14159rad)
  LinkedObject = -> Shape
  Placement = pos=(59.4,15.4,-2) rot=(0.707107,0.707107,0;3.14159rad)
FEATURE [App::Link] R1_R_0603_1608Metric_ed6f3b55dae2_ln_028  label="R52_R_0603_1608Metric_1314e578b8fa"
  LinkPlacement = pos=(26.75,6.65,-2) rot=(0.92388,-0.382683,0;3.14159rad)
  LinkedObject = -> Shape001
  Placement = pos=(26.75,6.65,-2) rot=(0.92388,-0.382683,0;3.14159rad)
FEATURE [App::Link] R1_R_0603_1608Metric_ed6f3b55dae2_ln_029  label="R59_R_0603_1608Metric_51d35e5e8522"
  LinkPlacement = pos=(11.45,7.3,-2) rot=(1,0,0;3.14159rad)
  LinkedObject = -> Shape001
  Placement = pos=(11.45,7.3,-2) rot=(1,0,0;3.14159rad)
FEATURE [App::Link] Y3_Crystal_HC49_U_Vertical_0fe1bbda450f_ln_  label="Y1_Crystal_HC49-U_Vertical_8a092cbe764f"
  LinkPlacement = pos=(2.85906,21.3,-2) rot=(1,0,0;3.14159rad)
  LinkedObject = -> Shape007
  Placement = pos=(2.85906,21.3,-2) rot=(1,0,0;3.14159rad)
FEATURE [App::Link] R1_R_0603_1608Metric_ed6f3b55dae2_ln_030  label="R9_R_0603_1608Metric_e8e6f4d4817b"
  LinkPlacement = pos=(52.55,14.9,-2) rot=(0.707107,-0.707107,0;3.14159rad)
  LinkedObject = -> Shape001
  Placement = pos=(52.55,14.9,-2) rot=(0.707107,-0.707107,0;3.14159rad)
FEATURE [App::Link] C6_C_0603_1608Metric_e4ffc2d5bdca_ln_011  label="C14_C_0603_1608Metric_0866816aecf6"
  LinkPlacement = pos=(12.5,26.2,-2) rot=(1,0,0;3.14159rad)
  LinkedObject = -> Shape
  Placement = pos=(12.5,26.2,-2) rot=(1,0,0;3.14159rad)
FEATURE [Part::Feature] Shape009  label="J3_PinHeader_1x13_P254mm_Vertical_SMD_Pin1Left_9baea8a7431d"
  Placement = pos=(16.8,9.7,-2) rot=(0.707107,-0.707107,0;3.14159rad)
  shape: bbox 33.02 x 5 x 9.3 mm, 355 faces (baked)
FEATURE [App::Link] C6_C_0603_1608Metric_e4ffc2d5bdca_ln_012  label="C13_C_0603_1608Metric_7b6bf5430122"
  LinkPlacement = pos=(18.275,17.1,-2) rot=(0,1,0;3.14159rad)
  LinkedObject = -> Shape
  Placement = pos=(18.275,17.1,-2) rot=(0,1,0;3.14159rad)
FEATURE [App::Link] R1_R_0603_1608Metric_ed6f3b55dae2_ln_031  label="R8_R_0603_1608Metric_03eb6692b740"
  LinkPlacement = pos=(22.3,13.7,-2) rot=(0,1,0;3.14159rad)
  LinkedObject = -> Shape001
  Placement = pos=(22.3,13.7,-2) rot=(0,1,0;3.14159rad)
FEATURE [Part::Feature] Shape010  label="JP5_PinHeader_1x03_P254mm_Vertical_SMD_Pin1Left_52619bf62036"
  Placement = pos=(15.8,21.3,-2) rot=(0.707107,-0.707107,0;3.14159rad)
  shape: bbox 7.62 x 5 x 9.3 mm, 85 faces (baked)
FEATURE [App::Link] C6_C_0603_1608Metric_e4ffc2d5bdca_ln_013  label="C9_C_0603_1608Metric_9afa2d7164e9"
  LinkPlacement = pos=(42.5,6.8,-2) rot=(0.707107,0.707107,0;3.14159rad)
  LinkedObject = -> Shape
  Placement = pos=(42.5,6.8,-2) rot=(0.707107,0.707107,0;3.14159rad)
FEATURE [App::Link] C6_C_0603_1608Metric_e4ffc2d5bdca_ln_014  label="C4_C_0603_1608Metric_4d1428f5722c"
  LinkPlacement = pos=(52.75,17.8,-2) rot=(0,1,0;3.14159rad)
  LinkedObject = -> Shape
  Placement = pos=(52.75,17.8,-2) rot=(0,1,0;3.14159rad)
FEATURE [App::Link] R1_R_0603_1608Metric_ed6f3b55dae2_ln_032  label="R3_R_0603_1608Metric_36257eaa7fe0"
  LinkPlacement = pos=(45.2,19.3,-2) rot=(0,1,0;3.14159rad)
  LinkedObject = -> Shape001
  Placement = pos=(45.2,19.3,-2) rot=(0,1,0;3.14159rad)
FEATURE [App::Link] R1_R_0603_1608Metric_ed6f3b55dae2_ln_033  label="R55_R_0603_1608Metric_c16f27e9f752"
  LinkPlacement = pos=(6.7,7.3,-2) rot=(1,0,0;3.14159rad)
  LinkedObject = -> Shape001
  Placement = pos=(6.7,7.3,-2) rot=(1,0,0;3.14159rad)
FEATURE [App::Link] R1_R_0603_1608Metric_ed6f3b55dae2_ln_034  label="R11_R_0603_1608Metric_86f9d7e7f3b2"
  LinkPlacement = pos=(18.2,18.7,-2) rot=(0,1,0;3.14159rad)
  LinkedObject = -> Shape001
  Placement = pos=(18.2,18.7,-2) rot=(0,1,0;3.14159rad)
FEATURE [App::Part] Bot_a649
  Group = -> [R1_R_0603_1608Metric_ed6f3b55dae2_ln_010,R1_R_0603_1608Metric_ed6f3b55dae2_ln_011,R1_R_0603_1608Metric_ed6f3b55dae2_ln_012,C6_C_0603_1608Metric_e4ffc2d5bdca_ln_004,R1_R_0603_1608Metric_ed6f3b55dae2_ln_013,Shape003,R1_R_0603_1608Metric_ed6f3b55dae2_ln_014,R1_R_0603_1608Metric_ed6f3b55dae2_ln_015,Shape004,Shape005,L3_L_0805_2012Metric_7024b431f41a_ln_,R1_R_0603_1608Metric_ed6f3b55dae2_ln_016,+37 more]
  Origin = -> Origin004
FEATURE [Part::Feature] Part__Feature065  label="Chamfer007"
  Placement = pos=(-16,0,7.18) rot=(0,0,1;0rad)
  shape: bbox 58.4 x 17 x 5.19 mm, 18 faces (baked)
FEATURE [Part::Feature] Part__Feature066  label="Pins001"
  shape: bbox 56.21 x 3.05 x 4.6 mm, 448 faces, 32 solids (baked)
FEATURE [Part::Feature] Part__Feature067  label="Compound"
  shape: bbox 56.21 x 3.05 x 4.6 mm, 448 faces, 32 solids (baked)
FEATURE [App::Part] DIL_64
  Group = -> [Part__Feature065,Part__Feature066,Part__Feature067]
  Origin = -> Origin012
  Placement = pos=(31.2,16.45,3) rot=(0,0,1;0rad)
FEATURE [Part::Feature] pads_area023001  label="topPads_a649"
  Placement = pos=(-95.1,117.3,0.02) rot=(0,0,1;0rad)
  shape: bbox 60 x 29.1 x 2e-07 mm, 366 faces, 0 solids (baked)
FEATURE [Part::Feature] pads_area023055001  label="botPads_a649"
  Placement = pos=(-95.1,117.3,-2.02) rot=(0,0,1;0rad)
  shape: bbox 60 x 29.1 x 2e-07 mm, 433 faces, 0 solids (baked)
FEATURE [App::Part] Board_Geoms_a649
  Group = -> [Local_CS_a649,Pcb_a649,pads_area023001,pads_area023055001,PCB_Sketch_a649]
  Origin = -> Origin
FEATURE [Part::Feature] Part__Feature068  label="Leg1"
  Placement = pos=(0,-2.5,0) rot=(0,0,1;0rad)
  shape: bbox 3.3 x 0.5 x 0.975 mm, 29 faces (baked)
FEATURE [Part::Feature] Part__Feature069  label="Leg002"
  Placement = pos=(0,-3.5,0) rot=(0,0,1;0rad)
  shape: bbox 3.3 x 0.5 x 0.975 mm, 29 faces (baked)
FEATURE [Part::Feature] Part__Feature070  label="Leg003"
  Placement = pos=(0,-4.5,0) rot=(0,0,1;0rad)
  shape: bbox 3.3 x 0.5 x 0.975 mm, 29 faces (baked)
FEATURE [Part::Feature] Part__Feature071  label="Leg004"
  Placement = pos=(0,-5.5,0) rot=(0,0,1;0rad)
  shape: bbox 3.3 x 0.5 x 0.975 mm, 29 faces (baked)
FEATURE [Part::Feature] Part__Feature072  label="Leg005"
  Placement = pos=(0,-6.5,0) rot=(0,0,1;0rad)
  shape: bbox 3.3 x 0.5 x 0.975 mm, 29 faces (baked)
FEATURE [Part::Feature] Part__Feature073  label="Leg006"
  Placement = pos=(0,-7.5,0) rot=(0,0,1;0rad)
  shape: bbox 3.3 x 0.5 x 0.975 mm, 29 faces (baked)
FEATURE [App::Part] Legs
  Group = -> [Part__Feature068,Part__Feature069,Part__Feature070,Part__Feature071,Part__Feature072,Part__Feature073]
  Origin = -> Origin013
  Placement = pos=(0,2.5,0) rot=(0,0,1;0rad)
FEATURE [Part::Feature] Part__Feature074  label="Chamfer"
  Placement = pos=(-3,-0.75,0.475) rot=(0,0,1;0rad)
  shape: bbox 2.1 x 6.75 x 1.5 mm, 54 faces (baked)
FEATURE [App::Part] GCT_BC075_06
  Group = -> [Legs,Part__Feature074]
  Origin = -> Origin014
  Placement = pos=(20.1,2,0.02) rot=(0,0,1;1.5708rad)
FEATURE [Part::Feature] Part__Feature075  label="Chamfer008"
  Placement = pos=(-3,-4.75,0.475) rot=(0,0,1;0rad)
  shape: bbox 2.1 x 10.75 x 1.5 mm, 86 faces (baked)
FEATURE [Part::Feature] Part__Feature076  label="Leg007"
  shape: bbox 3.3 x 0.5 x 0.975 mm, 28 faces (baked)
FEATURE [Part::Feature] Part__Feature077  label="Leg008"
  Placement = pos=(0,-1,0) rot=(0,0,1;0rad)
  shape: bbox 3.3 x 0.5 x 0.975 mm, 28 faces (baked)
FEATURE [Part::Feature] Part__Feature078  label="Leg009"
  Placement = pos=(0,-2,0) rot=(0,0,1;0rad)
  shape: bbox 3.3 x 0.5 x 0.975 mm, 28 faces (baked)
FEATURE [Part::Feature] Part__Feature079  label="Leg010"
  Placement = pos=(0,-3,0) rot=(0,0,1;0rad)
  shape: bbox 3.3 x 0.5 x 0.975 mm, 28 faces (baked)
FEATURE [Part::Feature] Part__Feature080  label="Leg011"
  Placement = pos=(0,-4,0) rot=(0,0,1;0rad)
  shape: bbox 3.3 x 0.5 x 0.975 mm, 28 faces (baked)
FEATURE [Part::Feature] Part__Feature081  label="Leg012"
  Placement = pos=(0,-5,0) rot=(0,0,1;0rad)
  shape: bbox 3.3 x 0.5 x 0.975 mm, 28 faces (baked)
FEATURE [Part::Feature] Part__Feature082  label="Leg013"
  Placement = pos=(0,-6,0) rot=(0,0,1;0rad)
  shape: bbox 3.3 x 0.5 x 0.975 mm, 28 faces (baked)
FEATURE [Part::Feature] Part__Feature083  label="Leg014"
  Placement = pos=(0,-7,0) rot=(0,0,1;0rad)
  shape: bbox 3.3 x 0.5 x 0.975 mm, 28 faces (baked)
FEATURE [Part::Feature] Part__Feature084  label="Leg015"
  Placement = pos=(0,-8,0) rot=(0,0,1;0rad)
  shape: bbox 3.3 x 0.5 x 0.975 mm, 28 faces (baked)
FEATURE [Part::Feature] Part__Feature085  label="Leg016"
  Placement = pos=(0,-9,0) rot=(0,0,1;0rad)
  shape: bbox 3.3 x 0.5 x 0.975 mm, 28 faces (baked)
FEATURE [App::Part] Legs001
  Group = -> [Part__Feature076,Part__Feature077,Part__Feature078,Part__Feature079,Part__Feature080,Part__Feature081,Part__Feature082,Part__Feature083,Part__Feature084,Part__Feature085]
  Origin = -> Origin015
FEATURE [App::Part] GCT_BC075_10
  Group = -> [Part__Feature075,Legs001]
  Origin = -> Origin016
  Placement = pos=(6.5,2,-1.975) rot=(0.707107,0.707107,0;3.14159rad)
FEATURE [Part::Feature] Part__Feature086  label="Chamfer009"
  Placement = pos=(-3,-4.75,0.475) rot=(0,0,1;0rad)
  shape: bbox 2.1 x 10.75 x 1.5 mm, 86 faces (baked)
FEATURE [Part::Feature] Part__Feature087  label="Leg017"
  shape: bbox 3.3 x 0.5 x 0.975 mm, 28 faces (baked)
FEATURE [Part::Feature] Part__Feature088  label="Leg018"
  Placement = pos=(0,-1,0) rot=(0,0,1;0rad)
  shape: bbox 3.3 x 0.5 x 0.975 mm, 28 faces (baked)
FEATURE [Part::Feature] Part__Feature089  label="Leg019"
  Placement = pos=(0,-2,0) rot=(0,0,1;0rad)
  shape: bbox 3.3 x 0.5 x 0.975 mm, 28 faces (baked)
FEATURE [Part::Feature] Part__Feature090  label="Leg020"
  Placement = pos=(0,-3,0) rot=(0,0,1;0rad)
  shape: bbox 3.3 x 0.5 x 0.975 mm, 28 faces (baked)
FEATURE [Part::Feature] Part__Feature091  label="Leg021"
  Placement = pos=(0,-4,0) rot=(0,0,1;0rad)
  shape: bbox 3.3 x 0.5 x 0.975 mm, 28 faces (baked)
FEATURE [Part::Feature] Part__Feature092  label="Leg022"
  Placement = pos=(0,-5,0) rot=(0,0,1;0rad)
  shape: bbox 3.3 x 0.5 x 0.975 mm, 28 faces (baked)
FEATURE [Part::Feature] Part__Feature093  label="Leg023"
  Placement = pos=(0,-6,0) rot=(0,0,1;0rad)
  shape: bbox 3.3 x 0.5 x 0.975 mm, 28 faces (baked)
FEATURE [Part::Feature] Part__Feature094  label="Leg024"
  Placement = pos=(0,-7,0) rot=(0,0,1;0rad)
  shape: bbox 3.3 x 0.5 x 0.975 mm, 28 faces (baked)
FEATURE [Part::Feature] Part__Feature095  label="Leg025"
  Placement = pos=(0,-8,0) rot=(0,0,1;0rad)
  shape: bbox 3.3 x 0.5 x 0.975 mm, 28 faces (baked)
FEATURE [Part::Feature] Part__Feature096  label="Leg026"
  Placement = pos=(0,-9,0) rot=(0,0,1;0rad)
  shape: bbox 3.3 x 0.5 x 0.975 mm, 28 faces (baked)
FEATURE [App::Part] Legs002
  Group = -> [Part__Feature087,Part__Feature088,Part__Feature089,Part__Feature090,Part__Feature091,Part__Feature092,Part__Feature093,Part__Feature094,Part__Feature095,Part__Feature096]
  Origin = -> Origin017
FEATURE [App::Part] GCT_BC075_011
  Group = -> [Part__Feature086,Legs002]
  Origin = -> Origin018
  Placement = pos=(18.1,2,-1.975) rot=(0.707107,0.707107,0;3.14159rad)
FEATURE [Part::Feature] Part__Feature097  label="Chamfer010"
  Placement = pos=(-3,-4.75,0.475) rot=(0,0,1;0rad)
  shape: bbox 2.1 x 10.75 x 1.5 mm, 86 faces (baked)
FEATURE [Part::Feature] Part__Feature098  label="Leg027"
  shape: bbox 3.3 x 0.5 x 0.975 mm, 28 faces (baked)
FEATURE [Part::Feature] Part__Feature099  label="Leg028"
  Placement = pos=(0,-1,0) rot=(0,0,1;0rad)
  shape: bbox 3.3 x 0.5 x 0.975 mm, 28 faces (baked)
FEATURE [Part::Feature] Part__Feature100  label="Leg029"
  Placement = pos=(0,-2,0) rot=(0,0,1;0rad)
  shape: bbox 3.3 x 0.5 x 0.975 mm, 28 faces (baked)
FEATURE [Part::Feature] Part__Feature101  label="Leg030"
  Placement = pos=(0,-3,0) rot=(0,0,1;0rad)
  shape: bbox 3.3 x 0.5 x 0.975 mm, 28 faces (baked)
FEATURE [Part::Feature] Part__Feature102  label="Leg031"
  Placement = pos=(0,-4,0) rot=(0,0,1;0rad)
  shape: bbox 3.3 x 0.5 x 0.975 mm, 28 faces (baked)
FEATURE [Part::Feature] Part__Feature103  label="Leg032"
  Placement = pos=(0,-5,0) rot=(0,0,1;0rad)
  shape: bbox 3.3 x 0.5 x 0.975 mm, 28 faces (baked)
FEATURE [Part::Feature] Part__Feature104  label="Leg033"
  Placement = pos=(0,-6,0) rot=(0,0,1;0rad)
  shape: bbox 3.3 x 0.5 x 0.975 mm, 28 faces (baked)
FEATURE [Part::Feature] Part__Feature105  label="Leg034"
  Placement = pos=(0,-7,0) rot=(0,0,1;0rad)
  shape: bbox 3.3 x 0.5 x 0.975 mm, 28 faces (baked)
FEATURE [Part::Feature] Part__Feature106  label="Leg035"
  Placement = pos=(0,-8,0) rot=(0,0,1;0rad)
  shape: bbox 3.3 x 0.5 x 0.975 mm, 28 faces (baked)
FEATURE [Part::Feature] Part__Feature107  label="Leg036"
  Placement = pos=(0,-9,0) rot=(0,0,1;0rad)
  shape: bbox 3.3 x 0.5 x 0.975 mm, 28 faces (baked)
FEATURE [App::Part] Legs003
  Group = -> [Part__Feature098,Part__Feature099,Part__Feature100,Part__Feature101,Part__Feature102,Part__Feature103,Part__Feature104,Part__Feature105,Part__Feature106,Part__Feature107]
  Origin = -> Origin019
FEATURE [App::Part] GCT_BC075_012
  Group = -> [Part__Feature097,Legs003]
  Origin = -> Origin020
  Placement = pos=(29.7,2,-1.975) rot=(0.707107,0.707107,0;3.14159rad)
FEATURE [Part::Feature] Part__Feature108  label="Chamfer011"
  Placement = pos=(-3,-4.75,0.475) rot=(0,0,1;0rad)
  shape: bbox 2.1 x 10.75 x 1.5 mm, 86 faces (baked)
FEATURE [Part::Feature] Part__Feature109  label="Leg037"
  shape: bbox 3.3 x 0.5 x 0.975 mm, 28 faces (baked)
FEATURE [Part::Feature] Part__Feature110  label="Leg038"
  Placement = pos=(0,-1,0) rot=(0,0,1;0rad)
  shape: bbox 3.3 x 0.5 x 0.975 mm, 28 faces (baked)
FEATURE [Part::Feature] Part__Feature111  label="Leg039"
  Placement = pos=(0,-2,0) rot=(0,0,1;0rad)
  shape: bbox 3.3 x 0.5 x 0.975 mm, 28 faces (baked)
FEATURE [Part::Feature] Part__Feature112  label="Leg040"
  Placement = pos=(0,-3,0) rot=(0,0,1;0rad)
  shape: bbox 3.3 x 0.5 x 0.975 mm, 28 faces (baked)
FEATURE [Part::Feature] Part__Feature113  label="Leg041"
  Placement = pos=(0,-4,0) rot=(0,0,1;0rad)
  shape: bbox 3.3 x 0.5 x 0.975 mm, 28 faces (baked)
FEATURE [Part::Feature] Part__Feature114  label="Leg042"
  Placement = pos=(0,-5,0) rot=(0,0,1;0rad)
  shape: bbox 3.3 x 0.5 x 0.975 mm, 28 faces (baked)
FEATURE [Part::Feature] Part__Feature115  label="Leg043"
  Placement = pos=(0,-6,0) rot=(0,0,1;0rad)
  shape: bbox 3.3 x 0.5 x 0.975 mm, 28 faces (baked)
FEATURE [Part::Feature] Part__Feature116  label="Leg044"
  Placement = pos=(0,-7,0) rot=(0,0,1;0rad)
  shape: bbox 3.3 x 0.5 x 0.975 mm, 28 faces (baked)
FEATURE [Part::Feature] Part__Feature117  label="Leg045"
  Placement = pos=(0,-8,0) rot=(0,0,1;0rad)
  shape: bbox 3.3 x 0.5 x 0.975 mm, 28 faces (baked)
FEATURE [Part::Feature] Part__Feature118  label="Leg046"
  Placement = pos=(0,-9,0) rot=(0,0,1;0rad)
  shape: bbox 3.3 x 0.5 x 0.975 mm, 28 faces (baked)
FEATURE [App::Part] Legs004
  Group = -> [Part__Feature109,Part__Feature110,Part__Feature111,Part__Feature112,Part__Feature113,Part__Feature114,Part__Feature115,Part__Feature116,Part__Feature117,Part__Feature118]
  Origin = -> Origin021
FEATURE [App::Part] GCT_BC075_013
  Group = -> [Part__Feature108,Legs004]
  Origin = -> Origin022
  Placement = pos=(50.5,2,-1.975) rot=(0.707107,0.707107,0;3.14159rad)
FEATURE [Part::Feature] Part__Feature119  label="Leg047"
  shape: bbox 3.3 x 0.5 x 0.975 mm, 29 faces (baked)
FEATURE [Part::Feature] Part__Feature120  label="Leg048"
  Placement = pos=(0,-1,0) rot=(0,0,1;0rad)
  shape: bbox 3.3 x 0.5 x 0.975 mm, 29 faces (baked)
FEATURE [Part::Feature] Part__Feature121  label="Leg049"
  Placement = pos=(0,-2,0) rot=(0,0,1;0rad)
  shape: bbox 3.3 x 0.5 x 0.975 mm, 29 faces (baked)
FEATURE [Part::Feature] Part__Feature122  label="Leg050"
  Placement = pos=(0,-3,0) rot=(0,0,1;0rad)
  shape: bbox 3.3 x 0.5 x 0.975 mm, 29 faces (baked)
FEATURE [Part::Feature] Part__Feature123  label="Leg051"
  Placement = pos=(0,-4,0) rot=(0,0,1;0rad)
  shape: bbox 3.3 x 0.5 x 0.975 mm, 29 faces (baked)
FEATURE [App::Part] Legs005
  Group = -> [Part__Feature119,Part__Feature120,Part__Feature121,Part__Feature122,Part__Feature123]
  Origin = -> Origin023
  Placement = pos=(0,-2.5,0) rot=(0,0,1;0rad)
FEATURE [Part::Feature] Part__Feature124  label="Plastic_casing"
  Placement = pos=(0,-2.5,0) rot=(0,0,1;0rad)
  shape: bbox 2.1 x 5.75 x 1.5 mm, 46 faces (baked)
FEATURE [App::Part] Unnamed  label="GCT_BC075_5-1"
  Group = -> [Legs005,Part__Feature124]
  Origin = -> Origin024
  Placement = pos=(42.1,2,0.025) rot=(0,0,1;1.5708rad)
FEATURE [Part::Feature] Part__Feature125  label="Leg052"
  shape: bbox 3.3 x 0.5 x 0.975 mm, 29 faces (baked)
FEATURE [Part::Feature] Part__Feature126  label="Leg053"
  Placement = pos=(0,-1,0) rot=(0,0,1;0rad)
  shape: bbox 3.3 x 0.5 x 0.975 mm, 29 faces (baked)
FEATURE [Part::Feature] Part__Feature127  label="Leg054"
  Placement = pos=(0,-2,0) rot=(0,0,1;0rad)
  shape: bbox 3.3 x 0.5 x 0.975 mm, 29 faces (baked)
FEATURE [Part::Feature] Part__Feature128  label="Leg055"
  Placement = pos=(0,-3,0) rot=(0,0,1;0rad)
  shape: bbox 3.3 x 0.5 x 0.975 mm, 29 faces (baked)
FEATURE [Part::Feature] Part__Feature129  label="Leg056"
  Placement = pos=(0,-4,0) rot=(0,0,1;0rad)
  shape: bbox 3.3 x 0.5 x 0.975 mm, 29 faces (baked)
FEATURE [App::Part] Legs006
  Group = -> [Part__Feature125,Part__Feature126,Part__Feature127,Part__Feature128,Part__Feature129]
  Origin = -> Origin025
  Placement = pos=(0,-2.5,0) rot=(0,0,1;0rad)
FEATURE [Part::Feature] Part__Feature130  label="Plastic_casing001"
  Placement = pos=(0,-2.5,0) rot=(0,0,1;0rad)
  shape: bbox 2.1 x 5.75 x 1.5 mm, 46 faces (baked)
FEATURE [App::Part] Unnamed001  label="GCT_BC075_5-002"
  Group = -> [Legs006,Part__Feature130]
  Origin = -> Origin026
  Placement = pos=(57.3,2,0.025) rot=(0,0,1;1.5708rad)
FEATURE [App::Part] Top_a649
  Group = -> [Mill_Max_117_43,Shape,Shape001,R1_R_0603_1608Metric_ed6f3b55dae2_ln_,R1_R_0603_1608Metric_ed6f3b55dae2_ln_001,R1_R_0603_1608Metric_ed6f3b55dae2_ln_002,R1_R_0603_1608Metric_ed6f3b55dae2_ln_003,R1_R_0603_1608Metric_ed6f3b55dae2_ln_004,C6_C_0603_1608Metric_e4ffc2d5bdca_ln_,R1_R_0603_1608Metric_ed6f3b55dae2_ln_005,C6_C_0603_1608Metric_e4ffc2d5bdca_ln_001,Shape002,+14 more]
  Origin = -> Origin003
FEATURE [App::Part] Step_Models_a649
  Group = -> [Top_a649,Bot_a649]
  Origin = -> Origin002
FEATURE [App::Part] Board_a649  label="Ultra-VDP"
  Group = -> [Board_Geoms_a649,Step_Models_a649]
  Origin = -> Origin001
